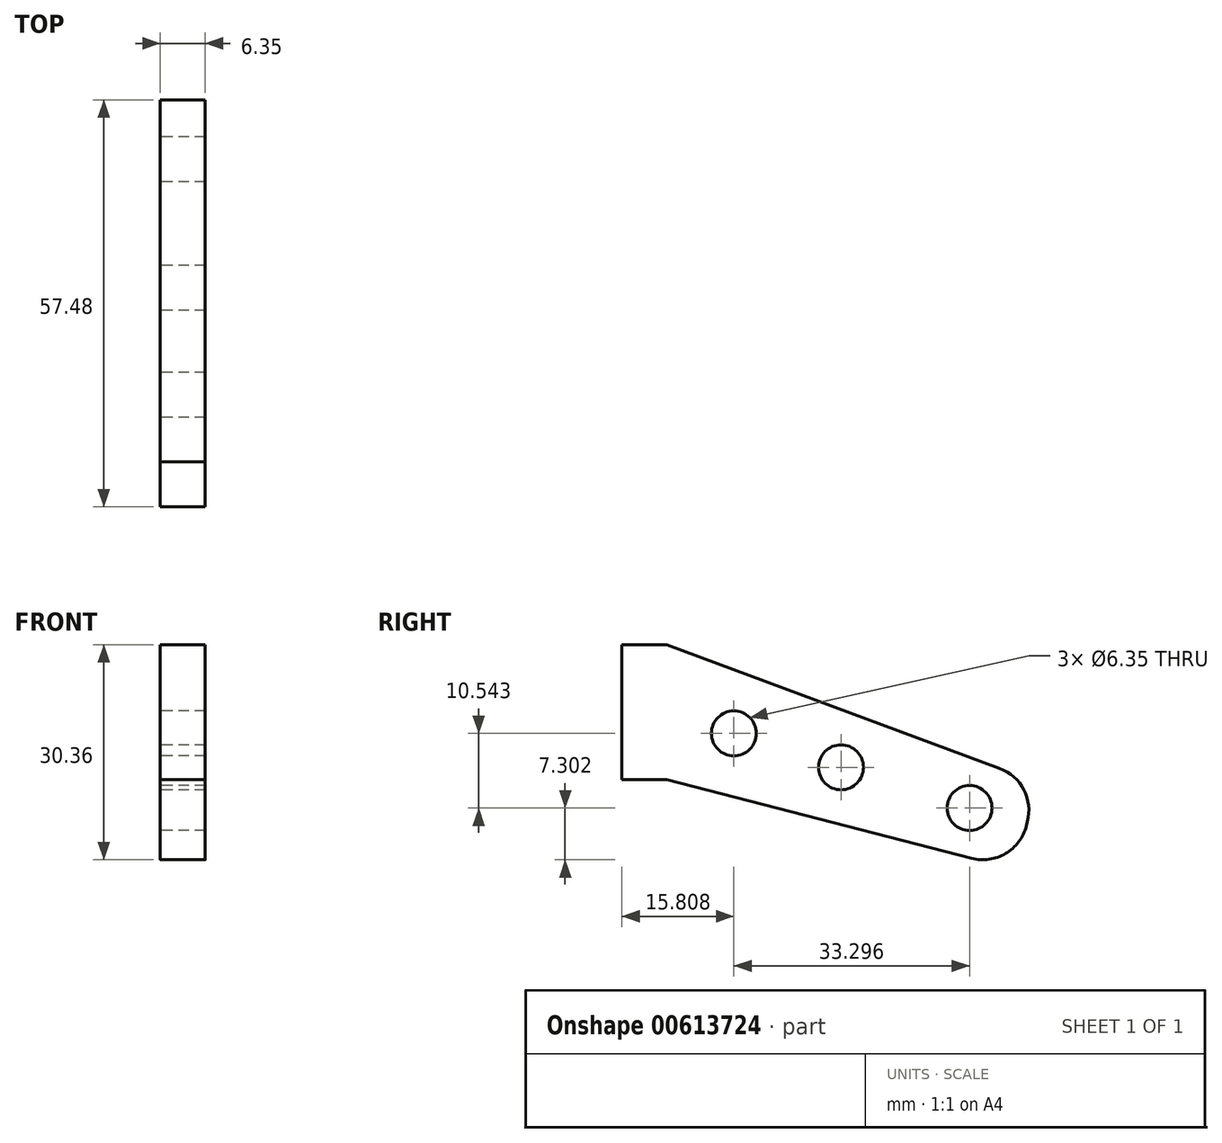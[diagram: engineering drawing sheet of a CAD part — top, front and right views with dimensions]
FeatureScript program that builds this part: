
annotation { "Feature Type Name" : "Feature", "Feature Type Description" : "" }
export const myFeature = defineFeature(function(context is Context, id is Id, definition is map)
    precondition{}
    {
        {
            var Q0;
            Q0=qCreatedBy(makeId("Right.planeOp"),FACE);
            var sketch = newSketch(context, id + "F0", { "sketchPlane" : qUnion([Q0])});
            skLineSegment(sketch, "E0.bottom", {"start": v(-37, -8.44) * mm, "end": v(-30.65, -8.44) * mm});
            skLineSegment(sketch, "E0.top", {"start": v(-37, -27.49) * mm, "end": v(-30.65, -27.49) * mm});
            skLineSegment(sketch, "E0.left", {"start": v(-37, -8.44) * mm, "end": v(-37, -27.49) * mm});
            skLineSegment(sketch, "E1", {"start": v(-30.65, -27.49) * mm, "end": v(12.39, -38.6) * mm});
            skLineSegment(sketch, "E2", {"start": v(20.12, -34.04) * mm, "end": v(20.28, -33.43) * mm});
            skLineSegment(sketch, "E3", {"start": v(-30.65, -8.44) * mm, "end": v(16.34, -25.9) * mm});
            skCircle(sketch, "E4", {"center": v(-6.06, -25.75) * mm, "radius": 3.18 * mm});
            skPoint(sketch, "E4.centerSnap0", {"position": v(-6.06, -33.84) * mm});
            skCircle(sketch, "E5", {"center": v(12.1, -31.5) * mm, "radius": 3.18 * mm});
            skCircle(sketch, "E6", {"center": v(-21.2, -20.96) * mm, "radius": 3.18 * mm});
            skPoint(sketch, "E7.visualSharp", {"position": v(21.71, -27.89) * mm});
            skArc(sketch, "E7.filletArc", {"start": v(20.28, -33.43) * mm, "mid": v(19.76, -28.9) * mm, "end": v(16.34, -25.9) * mm});
            skPoint(sketch, "E8.visualSharp", {"position": v(18.54, -40.19) * mm});
            skArc(sketch, "E8.filletArc", {"start": v(12.39, -38.6) * mm, "mid": v(17.2, -37.92) * mm, "end": v(20.12, -34.04) * mm});
            skSolve(sketch);
        }
        {
            var Q0;
            Q0=makeQuery(id+"F0.imprint","IMPRINT",FACE,{"disambiguationData":[TD([[makeQuery(id+"F0.imprint","IMPRINT",EDGE,{"derivedFrom":sQuery(id+"F0.wireOp",EDGE,"E0.bottom")}),-1.0]])]});
            extrude(context, id + "F1", {"entities" : qUnion([Q0]), "depth" : 6.35 * mm, "offsetDistance" : 25.4 * mm});
        }
    });
